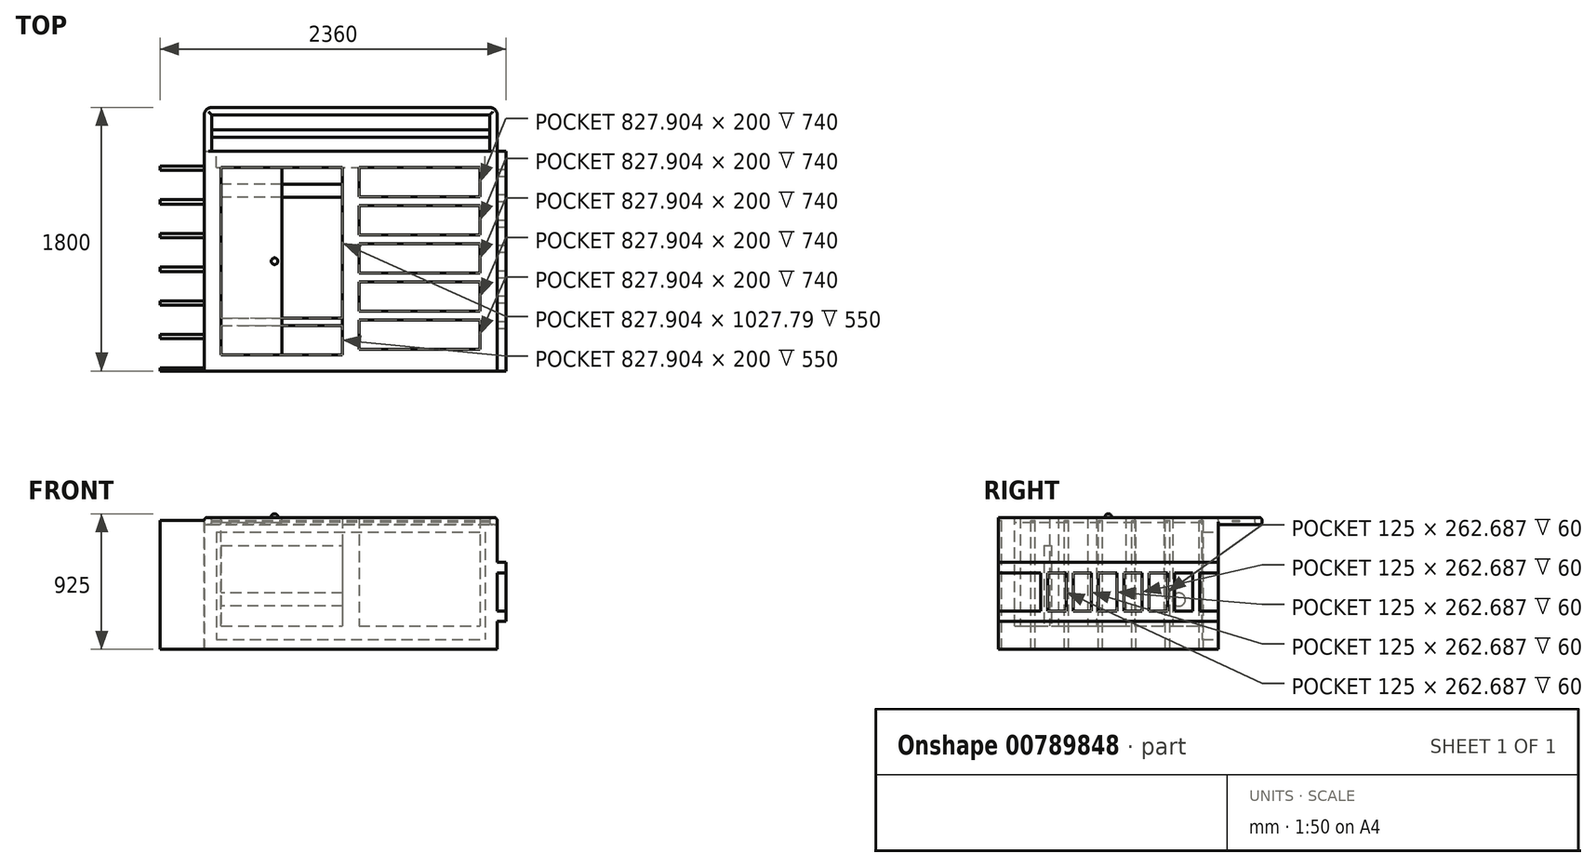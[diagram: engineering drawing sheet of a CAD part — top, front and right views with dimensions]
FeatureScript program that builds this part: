
annotation { "Feature Type Name" : "Feature", "Feature Type Description" : "" }
export const myFeature = defineFeature(function(context is Context, id is Id, definition is map)
    precondition{}
    {
        {
            var Q0;
            Q0=qCreatedBy(makeId("Top.planeOp"),FACE);
            var sketch = newSketch(context, id + "F0", { "sketchPlane" : qUnion([Q0])});
            skLineSegment(sketch, "E0.bottom", {"start": v(1000, -750) * mm, "end": v(-1000, -750) * mm});
            skLineSegment(sketch, "E0.top", {"start": v(1000, 750) * mm, "end": v(-1000, 750) * mm});
            skLineSegment(sketch, "E0.left", {"start": v(1000, -750) * mm, "end": v(1000, 750) * mm});
            skLineSegment(sketch, "E0.right", {"start": v(-1000, -750) * mm, "end": v(-1000, 750) * mm});
            skPoint(sketch, "E0.middle", {"position": v(0, 0) * mm});
            skSolve(sketch);
        }
        {
            var Q0;
            Q0 = qSketchRegion(id + "F0", true);
            extrude(context, id + "F1", {"entities" : qUnion([Q0]), "depth" : 900 * mm, "offsetDistance" : 25 * mm});
        }
        {
            var Q0;
            Q0=makeQuery(id+"F1.opExtrude","CAP_FACE",FACE,{"disambiguationData":[OSD([sQuery(id+"F0.wireOp",EDGE,"E0.bottom"),sQuery(id+"F0.wireOp",EDGE,"E0.top"),sQuery(id+"F0.wireOp",EDGE,"E0.left"),sQuery(id+"F0.wireOp",EDGE,"E0.right")])],"isStart":false});
            var sketch = newSketch(context, id + "F2", { "sketchPlane" : qUnion([Q0])});
            skLineSegment(sketch, "E1.bottom", {"start": v(-884.1, -638.9) * mm, "end": v(884.1, -638.9) * mm});
            skLineSegment(sketch, "E1.top", {"start": v(-884.1, 638.9) * mm, "end": v(884.1, 638.9) * mm});
            skLineSegment(sketch, "E1.left", {"start": v(-884.1, -638.9) * mm, "end": v(-884.1, 638.9) * mm});
            skLineSegment(sketch, "E1.right", {"start": v(884.1, -638.9) * mm, "end": v(884.1, 638.9) * mm});
            skPoint(sketch, "E1.middle", {"position": v(0, 0) * mm});
            skSolve(sketch);
        }
        {
            var Q0;
            Q0=makeQuery(id+"F2.imprint","IMPRINT",FACE,{"disambiguationData":[TD([[makeQuery(id+"F2.imprint","IMPRINT",EDGE,{"derivedFrom":sQuery(id+"F2.wireOp",EDGE,"E1.bottom")}),1.0]])]});
            extrude(context, id + "F3", {"entities" : qUnion([Q0]), "operationType" : NewBodyOperationType.REMOVE, "oppositeDirection" : true, "depth" : 740 * mm, "offsetDistance" : 25 * mm});
        }
        {
            var Q0;
            Q0=makeQuery(id+"F3.boolean.opBoolean","COPY",FACE,{"derivedFrom":makeQuery(id+"F3.opExtrude","CAP_FACE",FACE,{"disambiguationData":[OSD([sQuery(id+"F2.wireOp",EDGE,"E1.bottom"),sQuery(id+"F2.wireOp",EDGE,"E1.top"),sQuery(id+"F2.wireOp",EDGE,"E1.left"),sQuery(id+"F2.wireOp",EDGE,"E1.right")])],"isStart":false})});
            var sketch = newSketch(context, id + "F4", { "sketchPlane" : qUnion([Q0])});
            skLineSegment(sketch, "E2.bottom", {"start": v(-56.19, -638.9) * mm, "end": v(56.19, -638.9) * mm});
            skLineSegment(sketch, "E2.top", {"start": v(-56.19, 638.9) * mm, "end": v(56.19, 638.9) * mm});
            skLineSegment(sketch, "E2.left", {"start": v(-56.19, -638.9) * mm, "end": v(-56.19, 638.9) * mm});
            skLineSegment(sketch, "E2.right", {"start": v(56.19, -638.9) * mm, "end": v(56.19, 638.9) * mm});
            skPoint(sketch, "E2.middle", {"position": v(0, 0) * mm});
            skSolve(sketch);
        }
        {
            var Q0;
            Q0=makeQuery(id+"F4.imprint","IMPRINT",FACE,{"disambiguationData":[TD([[makeQuery(id+"F4.imprint","IMPRINT",EDGE,{"derivedFrom":sQuery(id+"F4.wireOp",EDGE,"E2.bottom")}),1.0]])]});
            extrude(context, id + "F5", {"entities" : qUnion([Q0]), "operationType" : NewBodyOperationType.ADD, "depth" : 740 * mm, "offsetDistance" : 25 * mm});
        }
        {
            var Q0;
            Q0=makeQuery(id+"F1.opExtrude","SWEPT_FACE",FACE,{"disambiguationData":[OSD([sQuery(id+"F0.wireOp",EDGE,"E0.top")])]});
            var sketch = newSketch(context, id + "F6", { "sketchPlane" : qUnion([Q0])});
            skLineSegment(sketch, "E3.bottom", {"start": v(-1000, 900) * mm, "end": v(-950, 900) * mm});
            skLineSegment(sketch, "E3.top", {"start": v(-1000, 850) * mm, "end": v(-950, 850) * mm});
            skLineSegment(sketch, "E3.left", {"start": v(-1000, 900) * mm, "end": v(-1000, 850) * mm});
            skLineSegment(sketch, "E3.right", {"start": v(-950, 900) * mm, "end": v(-950, 850) * mm});
            skSolve(sketch);
        }
        {
            var Q0;
            Q0=makeQuery(id+"F6.imprint","IMPRINT",FACE,{"disambiguationData":[TD([[makeQuery(id+"F6.imprint","IMPRINT",EDGE,{"derivedFrom":sQuery(id+"F6.wireOp",EDGE,"E3.bottom")}),-1.0]])]});
            extrude(context, id + "F7", {"entities" : qUnion([Q0]), "operationType" : NewBodyOperationType.ADD, "depth" : 300 * mm, "offsetDistance" : 25 * mm});
        }
        {
            var Q0;
            Q0=makeQuery(id+"F7.opExtrude","SWEPT_FACE",FACE,{"disambiguationData":[OSD([sQuery(id+"F6.wireOp",EDGE,"E3.right")])]});
            var sketch = newSketch(context, id + "F8", { "sketchPlane" : qUnion([Q0])});
            skLineSegment(sketch, "E4.bottom", {"start": v(-1050, 850) * mm, "end": v(-1000, 850) * mm});
            skLineSegment(sketch, "E4.top", {"start": v(-1050, 900) * mm, "end": v(-1000, 900) * mm});
            skLineSegment(sketch, "E4.left", {"start": v(-1050, 850) * mm, "end": v(-1050, 900) * mm});
            skLineSegment(sketch, "E4.right", {"start": v(-1000, 850) * mm, "end": v(-1000, 900) * mm});
            skSolve(sketch);
        }
        {
            var Q0;
            Q0=makeQuery(id+"F1.opExtrude","SWEPT_FACE",FACE,{"disambiguationData":[OSD([sQuery(id+"F0.wireOp",EDGE,"E0.top")])]});
            var sketch = newSketch(context, id + "F9", { "sketchPlane" : qUnion([Q0])});
            skLineSegment(sketch, "E5.bottom", {"start": v(1000, 900) * mm, "end": v(950, 900) * mm});
            skLineSegment(sketch, "E5.top", {"start": v(1000, 850) * mm, "end": v(950, 850) * mm});
            skLineSegment(sketch, "E5.left", {"start": v(1000, 900) * mm, "end": v(1000, 850) * mm});
            skLineSegment(sketch, "E5.right", {"start": v(950, 900) * mm, "end": v(950, 850) * mm});
            skSolve(sketch);
        }
        {
            var Q0;
            Q0 = qSketchRegion(id + "F9", true);
            extrude(context, id + "F10", {"entities" : qUnion([Q0]), "operationType" : NewBodyOperationType.ADD, "depth" : 300 * mm, "offsetDistance" : 25 * mm});
        }
        {
            var Q0;
            Q0=makeQuery(id+"F8.imprint","IMPRINT",FACE,{"disambiguationData":[TD([[makeQuery(id+"F8.imprint","IMPRINT",EDGE,{"derivedFrom":sQuery(id+"F8.wireOp",EDGE,"E4.bottom")}),1.0]])]});
            extrude(context, id + "F11", {"entities" : qUnion([Q0]), "operationType" : NewBodyOperationType.ADD, "depth" : 1933 * mm, "offsetDistance" : 25 * mm});
        }
        {
            var Q0;
            Q0=makeQuery(id+"F7.opExtrude","CAP_EDGE",EDGE,{"disambiguationData":[OSD([sQuery(id+"F6.wireOp",EDGE,"E3.left")])],"isStart":false});
            fillet(context, id + "F12", {"entities" : qUnion([Q0]), "radius" : 50 * mm, "tangentPropagation" : true, "allowEdgeOverflow" : false});
        }
        {
            var Q0;
            Q0=makeQuery(id+"F10.opExtrude","CAP_EDGE",EDGE,{"disambiguationData":[OSD([sQuery(id+"F9.wireOp",EDGE,"E5.left")])],"isStart":false});
            fillet(context, id + "F13", {"entities" : qUnion([Q0]), "radius" : 50 * mm, "tangentPropagation" : true, "allowEdgeOverflow" : false});
        }
        {
            var Q0;
            Q0=makeQuery(id+"F10.opExtrude","SWEPT_EDGE",EDGE,{"disambiguationData":[OSD([sQuery(id+"F0.wireOp",EDGE,"E0.top"),sQuery(id+"F0.wireOp",EDGE,"E0.right"),sQuery(id+"F9.wireOp",EDGE,"E5.top"),sQuery(id+"F9.wireOp",EDGE,"E5.left")])]});
            var Q1;
            Q1=makeQuery(id+"F10.opExtrude","SWEPT_EDGE",EDGE,{"disambiguationData":[OSD([sQuery(id+"F0.wireOp",EDGE,"E0.top"),sQuery(id+"F9.wireOp",EDGE,"E5.bottom"),sQuery(id+"F9.wireOp",EDGE,"E5.right")])]});
            var Q2;
            Q2=makeQuery(id+"F10.opExtrude","SWEPT_EDGE",EDGE,{"disambiguationData":[OSD([sQuery(id+"F9.wireOp",EDGE,"E5.top"),sQuery(id+"F9.wireOp",EDGE,"E5.right")])]});
            var Q3;
            Q3=makeQuery(id+"F11.boolean.opBoolean","MERGE",EDGE,{"derivedFrom":[makeQuery(id+"F7.opExtrude","CAP_EDGE",EDGE,{"disambiguationData":[OSD([sQuery(id+"F6.wireOp",EDGE,"E3.bottom")])],"isStart":false}),makeQuery(id+"F10.opExtrude","CAP_EDGE",EDGE,{"disambiguationData":[OSD([sQuery(id+"F9.wireOp",EDGE,"E5.bottom")])],"isStart":false}),makeQuery(id+"F11.opExtrude","SWEPT_EDGE",EDGE,{"disambiguationData":[OSD([sQuery(id+"F8.wireOp",EDGE,"E4.top"),sQuery(id+"F8.wireOp",EDGE,"E4.left")])]})]});
            var Q4;
            Q4=makeQuery(id+"F11.opExtrude","SWEPT_EDGE",EDGE,{"disambiguationData":[OSD([sQuery(id+"F0.wireOp",EDGE,"E0.top"),sQuery(id+"F6.wireOp",EDGE,"E3.bottom"),sQuery(id+"F6.wireOp",EDGE,"E3.right"),sQuery(id+"F8.wireOp",EDGE,"E4.top"),sQuery(id+"F8.wireOp",EDGE,"E4.right")])]});
            var Q5;
            Q5=makeQuery(id+"F11.boolean.opBoolean","MERGE",EDGE,{"derivedFrom":[makeQuery(id+"F7.opExtrude","CAP_EDGE",EDGE,{"disambiguationData":[OSD([sQuery(id+"F6.wireOp",EDGE,"E3.top")])],"isStart":false}),makeQuery(id+"F10.opExtrude","CAP_EDGE",EDGE,{"disambiguationData":[OSD([sQuery(id+"F9.wireOp",EDGE,"E5.top")])],"isStart":false}),makeQuery(id+"F11.opExtrude","SWEPT_EDGE",EDGE,{"disambiguationData":[OSD([sQuery(id+"F8.wireOp",EDGE,"E4.bottom"),sQuery(id+"F8.wireOp",EDGE,"E4.left")])]})]});
            var Q6;
            Q6=makeQuery(id+"F11.opExtrude","SWEPT_EDGE",EDGE,{"disambiguationData":[OSD([sQuery(id+"F6.wireOp",EDGE,"E3.top"),sQuery(id+"F6.wireOp",EDGE,"E3.right"),sQuery(id+"F8.wireOp",EDGE,"E4.bottom"),sQuery(id+"F8.wireOp",EDGE,"E4.right")])]});
            var Q7;
            Q7=makeQuery(id+"F7.opExtrude","SWEPT_EDGE",EDGE,{"disambiguationData":[OSD([sQuery(id+"F6.wireOp",EDGE,"E3.top"),sQuery(id+"F6.wireOp",EDGE,"E3.right")])]});
            var Q8;
            Q8=makeQuery(id+"F7.opExtrude","SWEPT_EDGE",EDGE,{"disambiguationData":[OSD([sQuery(id+"F0.wireOp",EDGE,"E0.top"),sQuery(id+"F6.wireOp",EDGE,"E3.bottom"),sQuery(id+"F6.wireOp",EDGE,"E3.right")])]});
            fillet(context, id + "F14", {"entities" : qUnion([Q0, Q1, Q2, Q3, Q4, Q5, Q6, Q7, Q8]), "radius" : 20 * mm, "tangentPropagation" : true, "allowEdgeOverflow" : false});
        }
        {
            var Q0;
            Q0=makeQuery(id+"F7.boolean.opBoolean","MERGE",FACE,{"derivedFrom":[makeQuery(id+"F1.opExtrude","SWEPT_FACE",FACE,{"disambiguationData":[OSD([sQuery(id+"F0.wireOp",EDGE,"E0.left")])]}),makeQuery(id+"F7.opExtrude","SWEPT_FACE",FACE,{"disambiguationData":[OSD([sQuery(id+"F6.wireOp",EDGE,"E3.left")])]})]});
            var sketch = newSketch(context, id + "F15", { "sketchPlane" : qUnion([Q0])});
            skLineSegment(sketch, "E6", {"start": v(871.27, 880) * mm, "end": v(871.27, 870) * mm});
            skCircle(sketch, "E7", {"center": v(871.27, 875) * mm, "radius": 25 * mm});
            skSolve(sketch);
        }
        {
            var Q0;
            {var subQ0=sQuery(id+"F15.wireOp",EDGE,"E6");Q0=makeQuery(id+"F15.imprint","IMPRINT",FACE,{"disambiguationData":[TD([[makeQuery(id+"F15.imprint","IMPRINT",EDGE,{"derivedFrom":subQ0}),1.0]])]});}
            var Q1;
            {var subQ0=sQuery(id+"F15.wireOp",EDGE,"E6");Q1=makeQuery(id+"F15.imprint","IMPRINT",FACE,{"disambiguationData":[TD([[makeQuery(id+"F15.imprint","IMPRINT",EDGE,{"derivedFrom":subQ0}),-1.0]])]});}
            var Q2;
            {var subQ0=sQuery(id+"F15.wireOp",EDGE,"E7");var subQ1=sQuery(id+"F6.wireOp",EDGE,"E3.left");var subQ2=sQuery(id+"F0.wireOp",EDGE,"E0.left");var subQ3=makeQuery(id+"F14.opFillet","BLEND_EDGE",EDGE,{"blendedFrom":[makeQuery(id+"F7.boolean.opBoolean","MERGE",EDGE,{"derivedFrom":[makeQuery(id+"F1.opExtrude","CAP_EDGE",EDGE,{"disambiguationData":[OSD([subQ2])],"isStart":false}),makeQuery(id+"F7.opExtrude","SWEPT_EDGE",EDGE,{"disambiguationData":[OSD([sQuery(id+"F6.wireOp",EDGE,"E3.bottom"),subQ1])]})]}),makeQuery(id+"F7.boolean.opBoolean","MERGE",FACE,{"derivedFrom":[makeQuery(id+"F1.opExtrude","SWEPT_FACE",FACE,{"disambiguationData":[OSD([subQ2])]}),makeQuery(id+"F7.opExtrude","SWEPT_FACE",FACE,{"disambiguationData":[OSD([subQ1])]})]})],"blendedInto":[makeQuery(id+"F7.boolean.opBoolean","MERGE",FACE,{"derivedFrom":[makeQuery(id+"F1.opExtrude","SWEPT_FACE",FACE,{"disambiguationData":[OSD([subQ2])]}),makeQuery(id+"F7.opExtrude","SWEPT_FACE",FACE,{"disambiguationData":[OSD([subQ1])]})]})]});var subQ4=makeQuery(id+"F15.imprint","INTERSECT",VERTEX,{"disambiguationData":[OD(0.0)],"derivedFrom":[subQ3,subQ0]});Q2=makeQuery(id+"F15.imprint","IMPRINT",FACE,{"disambiguationData":[TD([[makeQuery(id+"F15.imprint","IMPRINT",EDGE,{"disambiguationData":[TD([[subQ4,1.0]])],"derivedFrom":subQ0}),1.0]])]});}
            var Q3;
            {var subQ0=sQuery(id+"F15.wireOp",EDGE,"E7");var subQ1=sQuery(id+"F6.wireOp",EDGE,"E3.left");var subQ2=sQuery(id+"F0.wireOp",EDGE,"E0.left");var subQ3=makeQuery(id+"F14.opFillet","BLEND_EDGE",EDGE,{"blendedFrom":[makeQuery(id+"F7.opExtrude","SWEPT_EDGE",EDGE,{"disambiguationData":[OSD([sQuery(id+"F0.wireOp",EDGE,"E0.top"),subQ2,sQuery(id+"F6.wireOp",EDGE,"E3.top"),subQ1])]}),makeQuery(id+"F7.boolean.opBoolean","MERGE",FACE,{"derivedFrom":[makeQuery(id+"F1.opExtrude","SWEPT_FACE",FACE,{"disambiguationData":[OSD([subQ2])]}),makeQuery(id+"F7.opExtrude","SWEPT_FACE",FACE,{"disambiguationData":[OSD([subQ1])]})]})],"blendedInto":[makeQuery(id+"F7.boolean.opBoolean","MERGE",FACE,{"derivedFrom":[makeQuery(id+"F1.opExtrude","SWEPT_FACE",FACE,{"disambiguationData":[OSD([subQ2])]}),makeQuery(id+"F7.opExtrude","SWEPT_FACE",FACE,{"disambiguationData":[OSD([subQ1])]})]})]});var subQ4=makeQuery(id+"F15.imprint","INTERSECT",VERTEX,{"disambiguationData":[OD(0.0)],"derivedFrom":[subQ3,subQ0]});Q3=makeQuery(id+"F15.imprint","IMPRINT",FACE,{"disambiguationData":[TD([[makeQuery(id+"F15.imprint","IMPRINT",EDGE,{"disambiguationData":[TD([[subQ4,-1.0]])],"derivedFrom":subQ0}),1.0]])]});}
            extrude(context, id + "F16", {"entities" : qUnion([Q0, Q1, Q2, Q3]), "operationType" : NewBodyOperationType.ADD, "oppositeDirection" : true, "depth" : 2000 * mm, "offsetDistance" : 25 * mm});
        }
        {
            var Q0;
            Q0=makeQuery(id+"F16.boolean.opBoolean","MERGE",FACE,{"derivedFrom":[makeQuery(id+"F10.boolean.opBoolean","MERGE",FACE,{"derivedFrom":[makeQuery(id+"F1.opExtrude","SWEPT_FACE",FACE,{"disambiguationData":[OSD([sQuery(id+"F0.wireOp",EDGE,"E0.right")])]}),makeQuery(id+"F10.opExtrude","SWEPT_FACE",FACE,{"disambiguationData":[OSD([sQuery(id+"F9.wireOp",EDGE,"E5.left")])]})]}),makeQuery(id+"F16.opExtrude","CAP_FACE",FACE,{"disambiguationData":[OSD([sQuery(id+"F15.wireOp",EDGE,"E7")])],"isStart":false})]});
            var sketch = newSketch(context, id + "F17", { "sketchPlane" : qUnion([Q0])});
            skLineSegment(sketch, "E8.bottom", {"start": v(-650, 0) * mm, "end": v(-620, 0) * mm});
            skLineSegment(sketch, "E8.top", {"start": v(-650, 880) * mm, "end": v(-620, 880) * mm});
            skLineSegment(sketch, "E8.left", {"start": v(-650, 0) * mm, "end": v(-650, 880) * mm});
            skLineSegment(sketch, "E8.right", {"start": v(-620, 0) * mm, "end": v(-620, 880) * mm});
            skLineSegment(sketch, "E9.bottom", {"start": v(-420, 0) * mm, "end": v(-390, 0) * mm});
            skLineSegment(sketch, "E9.top", {"start": v(-420, 880) * mm, "end": v(-390, 880) * mm});
            skLineSegment(sketch, "E9.left", {"start": v(-420, 0) * mm, "end": v(-420, 880) * mm});
            skLineSegment(sketch, "E9.right", {"start": v(-390, 0) * mm, "end": v(-390, 880) * mm});
            skLineSegment(sketch, "E10.bottom", {"start": v(-190, 0) * mm, "end": v(-160, 0) * mm});
            skLineSegment(sketch, "E10.top", {"start": v(-190, 880) * mm, "end": v(-160, 880) * mm});
            skLineSegment(sketch, "E10.left", {"start": v(-190, 0) * mm, "end": v(-190, 880) * mm});
            skLineSegment(sketch, "E10.right", {"start": v(-160, 0) * mm, "end": v(-160, 880) * mm});
            skLineSegment(sketch, "E11.bottom", {"start": v(40, 0) * mm, "end": v(70, 0) * mm});
            skLineSegment(sketch, "E11.top", {"start": v(40, 880) * mm, "end": v(70, 880) * mm});
            skLineSegment(sketch, "E11.left", {"start": v(40, 0) * mm, "end": v(40, 880) * mm});
            skLineSegment(sketch, "E11.right", {"start": v(70, 0) * mm, "end": v(70, 880) * mm});
            skLineSegment(sketch, "E12.bottom", {"start": v(270, 0) * mm, "end": v(300, 0) * mm});
            skLineSegment(sketch, "E12.top", {"start": v(270, 880) * mm, "end": v(300, 880) * mm});
            skLineSegment(sketch, "E12.left", {"start": v(270, 0) * mm, "end": v(270, 880) * mm});
            skLineSegment(sketch, "E12.right", {"start": v(300, 0) * mm, "end": v(300, 880) * mm});
            skLineSegment(sketch, "E13.bottom", {"start": v(500, 0) * mm, "end": v(530, 0) * mm});
            skLineSegment(sketch, "E13.top", {"start": v(500, 880) * mm, "end": v(530, 880) * mm});
            skLineSegment(sketch, "E13.left", {"start": v(500, 0) * mm, "end": v(500, 880) * mm});
            skLineSegment(sketch, "E13.right", {"start": v(530, 0) * mm, "end": v(530, 880) * mm});
            skLineSegment(sketch, "E14.top", {"start": v(750, 880) * mm, "end": v(730, 880) * mm});
            skLineSegment(sketch, "E14.right", {"start": v(730, 0) * mm, "end": v(730, 880) * mm});
            skLineSegment(sketch, "E15", {"start": v(730, 0) * mm, "end": v(750, 0) * mm});
            skLineSegment(sketch, "E16", {"start": v(750, 0) * mm, "end": v(750, 880) * mm});
            skSolve(sketch);
        }
        {
            var Q0;
            Q0 = qSketchRegion(id + "F17", true);
            extrude(context, id + "F18", {"entities" : qUnion([Q0]), "operationType" : NewBodyOperationType.ADD, "depth" : 300 * mm, "offsetDistance" : 25 * mm});
        }
        {
            var Q0;
            Q0=makeQuery(id+"F3.boolean.opBoolean","COPY",FACE,{"derivedFrom":makeQuery(id+"F3.opExtrude","SWEPT_FACE",FACE,{"disambiguationData":[OSD([sQuery(id+"F2.wireOp",EDGE,"E1.left")])]})});
            var sketch = newSketch(context, id + "F19", { "sketchPlane" : qUnion([Q0])});
            skCircle(sketch, "E17", {"center": v(480.85, 339.84) * mm, "radius": 45 * mm});
            skSolve(sketch);
        }
        {
            var Q0;
            Q0=makeQuery(id+"F19.imprint","IMPRINT",FACE,{"disambiguationData":[TD([[makeQuery(id+"F19.imprint","IMPRINT",EDGE,{"derivedFrom":sQuery(id+"F19.wireOp",EDGE,"E17")}),1.0]])]});
            extrude(context, id + "F20", {"entities" : qUnion([Q0]), "operationType" : NewBodyOperationType.ADD, "depth" : 929 * mm, "offsetDistance" : 25 * mm});
        }
        {
            var Q0;
            Q0=makeQuery(id+"F1.opExtrude","SWEPT_FACE",FACE,{"disambiguationData":[OSD([sQuery(id+"F0.wireOp",EDGE,"E0.top")])]});
            var sketch = newSketch(context, id + "F21", { "sketchPlane" : qUnion([Q0])});
            skLineSegment(sketch, "E18.bottom", {"start": v(918.15, 801.15) * mm, "end": v(-918.15, 801.15) * mm});
            skLineSegment(sketch, "E18.top", {"start": v(918.15, 68.85) * mm, "end": v(-918.15, 68.85) * mm});
            skLineSegment(sketch, "E18.left", {"start": v(918.15, 801.15) * mm, "end": v(918.15, 68.85) * mm});
            skLineSegment(sketch, "E18.right", {"start": v(-918.15, 801.15) * mm, "end": v(-918.15, 68.85) * mm});
            skPoint(sketch, "E18.middle", {"position": v(0, 435) * mm});
            skPoint(sketch, "E18.middle.positionSnap0", {"position": v(-1000, 435) * mm});
            skPoint(sketch, "E18.centerSnap0", {"position": v(-1000, 435) * mm});
            skSolve(sketch);
        }
        {
            var Q0;
            Q0=makeQuery(id+"F21.imprint","IMPRINT",FACE,{"disambiguationData":[TD([[makeQuery(id+"F21.imprint","IMPRINT",EDGE,{"derivedFrom":sQuery(id+"F21.wireOp",EDGE,"E18.bottom")}),1.0]])]});
            extrude(context, id + "F22", {"entities" : qUnion([Q0]), "operationType" : NewBodyOperationType.REMOVE, "oppositeDirection" : true, "depth" : 110 * mm, "offsetDistance" : 25 * mm});
        }
        {
            var Q0;
            {var subQ0=sQuery(id+"F2.wireOp",EDGE,"E1.bottom");var subQ1=sQuery(id+"F2.wireOp",EDGE,"E1.top");var subQ2=sQuery(id+"F2.wireOp",EDGE,"E1.left");Q0=makeQuery(id+"F5.boolean.opBoolean","SPLIT",FACE,{"disambiguationData":[TD([makeQuery(id+"F3.boolean.opBoolean","COPY",FACE,{"derivedFrom":makeQuery(id+"F3.opExtrude","SWEPT_FACE",FACE,{"disambiguationData":[OSD([subQ2])]})})])],"derivedFrom":makeQuery(id+"F3.boolean.opBoolean","COPY",FACE,{"derivedFrom":makeQuery(id+"F3.opExtrude","CAP_FACE",FACE,{"disambiguationData":[OSD([subQ0,subQ1,subQ2,sQuery(id+"F2.wireOp",EDGE,"E1.right")])],"isStart":false})})});}
            var sketch = newSketch(context, id + "F23", { "sketchPlane" : qUnion([Q0])});
            skLineSegment(sketch, "E19", {"start": v(-884.1, -638.9) * mm, "end": v(-884.1, -438.9) * mm});
            skLineSegment(sketch, "E20.bottom", {"start": v(-884.1, -438.9) * mm, "end": v(-56.19, -438.9) * mm});
            skLineSegment(sketch, "E20.top", {"start": v(-884.1, -388.9) * mm, "end": v(-56.19, -388.9) * mm});
            skLineSegment(sketch, "E20.left", {"start": v(-884.1, -438.9) * mm, "end": v(-884.1, -388.9) * mm});
            skLineSegment(sketch, "E20.right", {"start": v(-56.19, -438.9) * mm, "end": v(-56.19, -388.9) * mm});
            skSolve(sketch);
        }
        {
            var Q0;
            Q0=makeQuery(id+"F23.imprint","IMPRINT",FACE,{"disambiguationData":[TD([[makeQuery(id+"F23.imprint","IMPRINT",EDGE,{"derivedFrom":sQuery(id+"F23.wireOp",EDGE,"E20.bottom")}),1.0]])]});
            extrude(context, id + "F24", {"entities" : qUnion([Q0]), "operationType" : NewBodyOperationType.ADD, "depth" : 550 * mm, "offsetDistance" : 25 * mm});
        }
        {
            var Q0;
            {var subQ0=sQuery(id+"F2.wireOp",EDGE,"E1.bottom");var subQ1=sQuery(id+"F2.wireOp",EDGE,"E1.top");var subQ2=sQuery(id+"F2.wireOp",EDGE,"E1.right");Q0=makeQuery(id+"F5.boolean.opBoolean","SPLIT",FACE,{"disambiguationData":[TD([makeQuery(id+"F3.boolean.opBoolean","COPY",FACE,{"derivedFrom":makeQuery(id+"F3.opExtrude","SWEPT_FACE",FACE,{"disambiguationData":[OSD([subQ2])]})})])],"derivedFrom":makeQuery(id+"F3.boolean.opBoolean","COPY",FACE,{"derivedFrom":makeQuery(id+"F3.opExtrude","CAP_FACE",FACE,{"disambiguationData":[OSD([subQ0,subQ1,sQuery(id+"F2.wireOp",EDGE,"E1.left"),subQ2])],"isStart":false})})});}
            var sketch = newSketch(context, id + "F25", { "sketchPlane" : qUnion([Q0])});
            skLineSegment(sketch, "E21", {"start": v(56.19, 638.9) * mm, "end": v(56.19, -638.9) * mm});
            skLineSegment(sketch, "E22", {"start": v(56.19, 638.9) * mm, "end": v(56.19, 438.9) * mm});
            skLineSegment(sketch, "E23.bottom", {"start": v(56.19, 438.9) * mm, "end": v(884.1, 438.9) * mm});
            skLineSegment(sketch, "E23.top", {"start": v(56.19, 378.9) * mm, "end": v(884.1, 378.9) * mm});
            skLineSegment(sketch, "E23.left", {"start": v(56.19, 438.9) * mm, "end": v(56.19, 378.9) * mm});
            skLineSegment(sketch, "E23.right", {"start": v(884.1, 438.9) * mm, "end": v(884.1, 378.9) * mm});
            skLineSegment(sketch, "E24", {"start": v(56.19, 378.9) * mm, "end": v(56.19, 178.9) * mm});
            skLineSegment(sketch, "E25.bottom", {"start": v(56.19, 178.9) * mm, "end": v(884.1, 178.9) * mm});
            skLineSegment(sketch, "E25.top", {"start": v(56.19, 118.9) * mm, "end": v(884.1, 118.9) * mm});
            skLineSegment(sketch, "E25.left", {"start": v(56.19, 178.9) * mm, "end": v(56.19, 118.9) * mm});
            skLineSegment(sketch, "E25.right", {"start": v(884.1, 178.9) * mm, "end": v(884.1, 118.9) * mm});
            skLineSegment(sketch, "E26", {"start": v(56.19, 118.9) * mm, "end": v(56.19, -81.1) * mm});
            skLineSegment(sketch, "E27.bottom", {"start": v(56.19, -81.1) * mm, "end": v(884.1, -81.1) * mm});
            skLineSegment(sketch, "E27.top", {"start": v(56.19, -141.1) * mm, "end": v(884.1, -141.1) * mm});
            skLineSegment(sketch, "E27.left", {"start": v(56.19, -81.1) * mm, "end": v(56.19, -141.1) * mm});
            skLineSegment(sketch, "E27.right", {"start": v(884.1, -81.1) * mm, "end": v(884.1, -141.1) * mm});
            skLineSegment(sketch, "E28", {"start": v(56.19, -141.1) * mm, "end": v(56.19, -341.1) * mm});
            skLineSegment(sketch, "E29.bottom", {"start": v(56.19, -341.1) * mm, "end": v(884.1, -341.1) * mm});
            skLineSegment(sketch, "E29.top", {"start": v(56.19, -401.1) * mm, "end": v(884.1, -401.1) * mm});
            skLineSegment(sketch, "E29.left", {"start": v(56.19, -341.1) * mm, "end": v(56.19, -401.1) * mm});
            skLineSegment(sketch, "E29.right", {"start": v(884.1, -341.1) * mm, "end": v(884.1, -401.1) * mm});
            skLineSegment(sketch, "E30", {"start": v(56.19, -401.1) * mm, "end": v(56.19, -601.1) * mm});
            skLineSegment(sketch, "E31.bottom", {"start": v(56.19, -601.1) * mm, "end": v(884.1, -601.1) * mm});
            skLineSegment(sketch, "E31.top", {"start": v(56.19, -638.9) * mm, "end": v(884.1, -638.9) * mm});
            skLineSegment(sketch, "E31.left", {"start": v(56.19, -601.1) * mm, "end": v(56.19, -638.9) * mm});
            skLineSegment(sketch, "E31.right", {"start": v(884.1, -601.1) * mm, "end": v(884.1, -638.9) * mm});
            skSolve(sketch);
        }
        {
            var Q0;
            Q0=makeQuery(id+"F25.imprint","IMPRINT",FACE,{"disambiguationData":[TD([[makeQuery(id+"F25.imprint","IMPRINT",EDGE,{"derivedFrom":sQuery(id+"F25.wireOp",EDGE,"E23.bottom")}),-1.0]])]});
            var Q1;
            Q1=makeQuery(id+"F25.imprint","IMPRINT",FACE,{"disambiguationData":[TD([[makeQuery(id+"F25.imprint","IMPRINT",EDGE,{"derivedFrom":sQuery(id+"F25.wireOp",EDGE,"E25.bottom")}),-1.0]])]});
            var Q2;
            Q2=makeQuery(id+"F25.imprint","IMPRINT",FACE,{"disambiguationData":[TD([[makeQuery(id+"F25.imprint","IMPRINT",EDGE,{"derivedFrom":sQuery(id+"F25.wireOp",EDGE,"E27.bottom")}),-1.0]])]});
            var Q3;
            Q3=makeQuery(id+"F25.imprint","IMPRINT",FACE,{"disambiguationData":[TD([[makeQuery(id+"F25.imprint","IMPRINT",EDGE,{"derivedFrom":sQuery(id+"F25.wireOp",EDGE,"E29.bottom")}),-1.0]])]});
            var Q4;
            Q4=makeQuery(id+"F25.imprint","IMPRINT",FACE,{"disambiguationData":[TD([[makeQuery(id+"F25.imprint","IMPRINT",EDGE,{"derivedFrom":sQuery(id+"F25.wireOp",EDGE,"E31.bottom")}),-1.0]])]});
            extrude(context, id + "F26", {"entities" : qUnion([Q0, Q1, Q2, Q3, Q4]), "operationType" : NewBodyOperationType.ADD, "depth" : 740 * mm, "offsetDistance" : 25 * mm});
        }
        {
            var Q0;
            Q0=makeQuery(id+"F3.boolean.opBoolean","COPY",FACE,{"derivedFrom":makeQuery(id+"F3.opExtrude","SWEPT_FACE",FACE,{"disambiguationData":[OSD([sQuery(id+"F2.wireOp",EDGE,"E1.left")])]})});
            var sketch = newSketch(context, id + "F27", { "sketchPlane" : qUnion([Q0])});
            skLineSegment(sketch, "E32.bottom", {"start": v(638.9, 900) * mm, "end": v(-638.9, 900) * mm});
            skLineSegment(sketch, "E32.top", {"start": v(638.9, 865) * mm, "end": v(-638.9, 865) * mm});
            skLineSegment(sketch, "E32.left", {"start": v(638.9, 900) * mm, "end": v(638.9, 865) * mm});
            skLineSegment(sketch, "E32.right", {"start": v(-638.9, 900) * mm, "end": v(-638.9, 865) * mm});
            skSolve(sketch);
        }
        {
            var Q0;
            Q0=makeQuery(id+"F27.imprint","IMPRINT",FACE,{"disambiguationData":[TD([[makeQuery(id+"F27.imprint","IMPRINT",EDGE,{"derivedFrom":sQuery(id+"F27.wireOp",EDGE,"E32.bottom")}),-1.0]])]});
            extrude(context, id + "F28", {"entities" : qUnion([Q0]), "depth" : 413.95 * mm, "offsetDistance" : 25 * mm});
        }
        {
            var Q0;
            Q0=makeQuery(id+"F28.opExtrude","SWEPT_FACE",FACE,{"disambiguationData":[OSD([sQuery(id+"F27.wireOp",EDGE,"E32.bottom")])]});
            var sketch = newSketch(context, id + "F29", { "sketchPlane" : qUnion([Q0])});
            skCircle(sketch, "E33", {"center": v(-520.14, 0) * mm, "radius": 22.5 * mm});
            skPoint(sketch, "E34.start.orphan", {"position": v(-470.14, 0) * mm});
            skSolve(sketch);
        }
        {
            var Q0;
            Q0=makeQuery(id+"F29.imprint","IMPRINT",FACE,{"disambiguationData":[TD([[makeQuery(id+"F29.imprint","IMPRINT",EDGE,{"derivedFrom":sQuery(id+"F29.wireOp",EDGE,"E33")}),1.0]])]});
            extrude(context, id + "F30", {"entities" : qUnion([Q0]), "operationType" : NewBodyOperationType.ADD, "depth" : 25 * mm, "offsetDistance" : 25 * mm});
        }
        {
            var Q0;
            Q0=makeQuery(id+"F30.opExtrude","CAP_EDGE",EDGE,{"disambiguationData":[OSD([sQuery(id+"F29.wireOp",EDGE,"E33")])],"isStart":false});
            fillet(context, id + "F31", {"entities" : qUnion([Q0]), "radius" : 20 * mm, "tangentPropagation" : true, "allowEdgeOverflow" : false});
        }
        {
            var Q0;
            Q0=makeQuery(id+"F16.boolean.opBoolean","MERGE",FACE,{"derivedFrom":[makeQuery(id+"F7.boolean.opBoolean","MERGE",FACE,{"derivedFrom":[makeQuery(id+"F1.opExtrude","SWEPT_FACE",FACE,{"disambiguationData":[OSD([sQuery(id+"F0.wireOp",EDGE,"E0.left")])]}),makeQuery(id+"F7.opExtrude","SWEPT_FACE",FACE,{"disambiguationData":[OSD([sQuery(id+"F6.wireOp",EDGE,"E3.left")])]})]}),makeQuery(id+"F16.opExtrude","CAP_FACE",FACE,{"disambiguationData":[OSD([sQuery(id+"F15.wireOp",EDGE,"E7")])],"isStart":true})]});
            var sketch = newSketch(context, id + "F32", { "sketchPlane" : qUnion([Q0])});
            skLineSegment(sketch, "E35", {"start": v(750, 592.84) * mm, "end": v(-750, 592.84) * mm});
            skLineSegment(sketch, "E36", {"start": v(-750, 522.84) * mm, "end": v(750, 522.84) * mm});
            skLineSegment(sketch, "E37", {"start": v(750, 522.84) * mm, "end": v(750, 592.84) * mm});
            skLineSegment(sketch, "E38", {"start": v(-750, 592.84) * mm, "end": v(-750, 522.84) * mm});
            skLineSegment(sketch, "E39", {"start": v(-750, 260.15) * mm, "end": v(452, 260.15) * mm});
            skLineSegment(sketch, "E40", {"start": v(750, 190.15) * mm, "end": v(-750, 190.15) * mm});
            skLineSegment(sketch, "E41", {"start": v(-750, 190.15) * mm, "end": v(-750, 260.15) * mm});
            skLineSegment(sketch, "E42", {"start": v(750, 190.15) * mm, "end": v(750, 260.15) * mm});
            skLineSegment(sketch, "E43", {"start": v(625, 522.84) * mm, "end": v(625, 260.15) * mm});
            skLineSegment(sketch, "E44", {"start": v(577, 260.15) * mm, "end": v(577, 522.84) * mm});
            skLineSegment(sketch, "E45", {"start": v(577, 260.15) * mm, "end": v(452, 260.15) * mm});
            skLineSegment(sketch, "E46", {"start": v(452, 260.15) * mm, "end": v(452, 522.84) * mm});
            skLineSegment(sketch, "E47", {"start": v(452, 260.15) * mm, "end": v(404, 260.15) * mm});
            skLineSegment(sketch, "E48", {"start": v(404, 260.15) * mm, "end": v(404, 522.84) * mm});
            skLineSegment(sketch, "E49", {"start": v(404, 260.15) * mm, "end": v(279, 260.15) * mm});
            skLineSegment(sketch, "E50", {"start": v(279, 260.15) * mm, "end": v(279, 522.84) * mm});
            skLineSegment(sketch, "E51", {"start": v(279, 522.84) * mm, "end": v(231, 522.84) * mm});
            skLineSegment(sketch, "E52", {"start": v(231, 522.84) * mm, "end": v(231, 260.15) * mm});
            skLineSegment(sketch, "E53", {"start": v(231, 260.15) * mm, "end": v(279, 260.15) * mm});
            skLineSegment(sketch, "E54", {"start": v(231, 522.84) * mm, "end": v(106, 522.84) * mm});
            skLineSegment(sketch, "E55", {"start": v(106, 522.84) * mm, "end": v(106, 260.15) * mm});
            skLineSegment(sketch, "E56", {"start": v(106, 260.15) * mm, "end": v(58, 260.15) * mm});
            skLineSegment(sketch, "E57", {"start": v(58, 260.15) * mm, "end": v(58, 522.84) * mm});
            skLineSegment(sketch, "E58", {"start": v(58, 522.84) * mm, "end": v(106, 522.84) * mm});
            skLineSegment(sketch, "E59", {"start": v(58, 522.84) * mm, "end": v(-67, 522.84) * mm});
            skLineSegment(sketch, "E60", {"start": v(-67, 522.84) * mm, "end": v(-67, 260.15) * mm});
            skLineSegment(sketch, "E61", {"start": v(-67, 260.15) * mm, "end": v(-115, 260.15) * mm});
            skLineSegment(sketch, "E62", {"start": v(-115, 260.15) * mm, "end": v(-115, 522.84) * mm});
            skLineSegment(sketch, "E63", {"start": v(-115, 522.84) * mm, "end": v(-67, 522.84) * mm});
            skLineSegment(sketch, "E64", {"start": v(-115, 522.84) * mm, "end": v(-240, 522.84) * mm});
            skLineSegment(sketch, "E65", {"start": v(-240, 522.84) * mm, "end": v(-240, 260.15) * mm});
            skLineSegment(sketch, "E66", {"start": v(-240, 260.15) * mm, "end": v(-288, 260.15) * mm});
            skLineSegment(sketch, "E67", {"start": v(-288, 260.15) * mm, "end": v(-288, 522.84) * mm});
            skLineSegment(sketch, "E68", {"start": v(-288, 522.84) * mm, "end": v(-240, 522.84) * mm});
            skLineSegment(sketch, "E69", {"start": v(-288, 522.84) * mm, "end": v(-413, 522.84) * mm});
            skLineSegment(sketch, "E70", {"start": v(-413, 522.84) * mm, "end": v(-413, 260.15) * mm});
            skLineSegment(sketch, "E71", {"start": v(-413, 260.15) * mm, "end": v(-461, 260.15) * mm});
            skLineSegment(sketch, "E72", {"start": v(-461, 260.15) * mm, "end": v(-461, 522.84) * mm});
            skLineSegment(sketch, "E73", {"start": v(-461, 522.84) * mm, "end": v(-413, 522.84) * mm});
            skLineSegment(sketch, "E74.trimOffspring", {"start": v(577, 260.15) * mm, "end": v(750, 260.15) * mm});
            skSolve(sketch);
        }
        {
            var Q0;
            {var subQ0=sQuery(id+"F32.wireOp",EDGE,"E43");Q0=makeQuery(id+"F32.imprint","IMPRINT",FACE,{"disambiguationData":[TD([[makeQuery(id+"F32.imprint","IMPRINT",EDGE,{"derivedFrom":subQ0}),-1.0]])]});}
            var Q1;
            {var subQ0=sQuery(id+"F32.wireOp",EDGE,"E46");Q1=makeQuery(id+"F32.imprint","IMPRINT",FACE,{"disambiguationData":[TD([[makeQuery(id+"F32.imprint","IMPRINT",EDGE,{"derivedFrom":subQ0}),1.0]])]});}
            var Q2;
            Q2=makeQuery(id+"F32.imprint","IMPRINT",FACE,{"disambiguationData":[TD([[makeQuery(id+"F32.imprint","IMPRINT",EDGE,{"derivedFrom":sQuery(id+"F32.wireOp",EDGE,"E50")}),1.0]])]});
            var Q3;
            Q3=makeQuery(id+"F32.imprint","IMPRINT",FACE,{"disambiguationData":[TD([[makeQuery(id+"F32.imprint","IMPRINT",EDGE,{"derivedFrom":sQuery(id+"F32.wireOp",EDGE,"E55")}),-1.0]])]});
            var Q4;
            Q4=makeQuery(id+"F32.imprint","IMPRINT",FACE,{"disambiguationData":[TD([[makeQuery(id+"F32.imprint","IMPRINT",EDGE,{"derivedFrom":sQuery(id+"F32.wireOp",EDGE,"E60")}),-1.0]])]});
            var Q5;
            Q5=makeQuery(id+"F32.imprint","IMPRINT",FACE,{"disambiguationData":[TD([[makeQuery(id+"F32.imprint","IMPRINT",EDGE,{"derivedFrom":sQuery(id+"F32.wireOp",EDGE,"E65")}),-1.0]])]});
            var Q6;
            Q6=makeQuery(id+"F32.imprint","IMPRINT",FACE,{"disambiguationData":[TD([[makeQuery(id+"F32.imprint","IMPRINT",EDGE,{"derivedFrom":sQuery(id+"F32.wireOp",EDGE,"E70")}),-1.0]])]});
            var Q7;
            Q7=makeQuery(id+"F32.imprint","IMPRINT",FACE,{"disambiguationData":[TD([[makeQuery(id+"F32.imprint","IMPRINT",EDGE,{"derivedFrom":sQuery(id+"F32.wireOp",EDGE,"E40")}),-1.0]])]});
            var Q8;
            Q8=makeQuery(id+"F32.imprint","IMPRINT",FACE,{"disambiguationData":[TD([[makeQuery(id+"F32.imprint","IMPRINT",EDGE,{"derivedFrom":sQuery(id+"F32.wireOp",EDGE,"E35")}),1.0]])]});
            extrude(context, id + "F33", {"entities" : qUnion([Q0, Q1, Q2, Q3, Q4, Q5, Q6, Q7, Q8]), "operationType" : NewBodyOperationType.ADD, "depth" : 60 * mm, "offsetDistance" : 25 * mm});
        }
    });
